annotation { "Feature Type Name" : "Feature", "Feature Type Description" : "" }
export const myFeature = defineFeature(function(context is Context, id is Id, definition is map)
    precondition{}
    {
        {
            var Q0;
            Q0=qCreatedBy(makeId("Top.planeOp"),FACE);
            var sketch = newSketch(context, id + "F0", { "sketchPlane" : qUnion([Q0])});
            skLineSegment(sketch, "E0.bottom", {"start": v(37.5, 37.5) * mm, "end": v(-37.5, 37.5) * mm});
            skLineSegment(sketch, "E0.top", {"start": v(37.5, -37.5) * mm, "end": v(-37.5, -37.5) * mm});
            skLineSegment(sketch, "E0.left", {"start": v(37.5, 37.5) * mm, "end": v(37.5, -37.5) * mm});
            skLineSegment(sketch, "E0.right", {"start": v(-37.5, 37.5) * mm, "end": v(-37.5, -37.5) * mm});
            skPoint(sketch, "E0.middle", {"position": v(0, 0) * mm});
            skPoint(sketch, "E1.visualSharp", {"position": v(-37.5, 37.5) * mm});
            skLineSegment(sketch, "E1.filletArc", {"start": v(-37.5, 37.5) * mm, "end": v(-37.5, 37.5) * mm});
            skPoint(sketch, "E2.visualSharp", {"position": v(37.5, 37.5) * mm});
            skLineSegment(sketch, "E2.filletArc", {"start": v(37.5, 37.5) * mm, "end": v(37.5, 37.5) * mm});
            skPoint(sketch, "E3.visualSharp", {"position": v(37.5, -37.5) * mm});
            skLineSegment(sketch, "E3.filletArc", {"start": v(37.5, -37.5) * mm, "end": v(37.5, -37.5) * mm});
            skPoint(sketch, "E4.visualSharp", {"position": v(-37.5, -37.5) * mm});
            skLineSegment(sketch, "E4.filletArc", {"start": v(-37.5, -37.5) * mm, "end": v(-37.5, -37.5) * mm});
            skCircle(sketch, "E5", {"center": v(0, 0) * mm, "radius": 18.5 * mm});
            skSolve(sketch);
        }
        {
            var Q0;
            Q0=makeQuery(id+"F0.imprint","IMPRINT",FACE,{"disambiguationData":[TD([[makeQuery(id+"F0.imprint","IMPRINT",EDGE,{"derivedFrom":sQuery(id+"F0.wireOp",EDGE,"E0.bottom")}),1.0]])]});
            extrude(context, id + "F1", {"entities" : qUnion([Q0]), "depth" : 1 * mm, "offsetDistance" : 25 * mm});
        }
        {
            var Q0;
            Q0=makeQuery(id+"F1.opExtrude","CAP_FACE",FACE,{"disambiguationData":[OSD([sQuery(id+"F0.wireOp",EDGE,"E0.bottom"),sQuery(id+"F0.wireOp",EDGE,"E0.top"),sQuery(id+"F0.wireOp",EDGE,"E0.left"),sQuery(id+"F0.wireOp",EDGE,"E0.right")])],"isStart":false});
            var sketch = newSketch(context, id + "F2", { "sketchPlane" : qUnion([Q0])});
            skText(sketch, "E6", { "text": "TAG NUMBER", "fontName": "OpenSans-Regular.ttf"});
            skText(sketch, "E7", { "text": "PUSH\nTO\nSTOP", "fontName": "OpenSans-Regular.ttf"});
            skLineSegment(sketch, "E8", {"start": v(0, 37.5) * mm, "end": v(0, 32.82) * mm, "construction": true});
            skText(sketch, "E9", { "text": "  PULL\n     TO\nRESET", "fontName": "OpenSans-Regular.ttf"});
            const initialGuessF2  = {"E6": [-0.0279, 0.02657, 1, 0, 0.00625], "E7": [-0.0365, 0.00844, 1, 0, 0.005], "E9": [0.01782, 0.00853, 1, 0, 0.005]};
            skSetInitialGuess(sketch, initialGuessF2);
            skSolve(sketch);
        }
        {
            var Q0;
            Q0 = qSketchRegion(id + "F2", true);
            extrude(context, id + "F3", {"entities" : qUnion([Q0]), "depth" : 1 * mm, "offsetDistance" : 25 * mm});
        }
    });